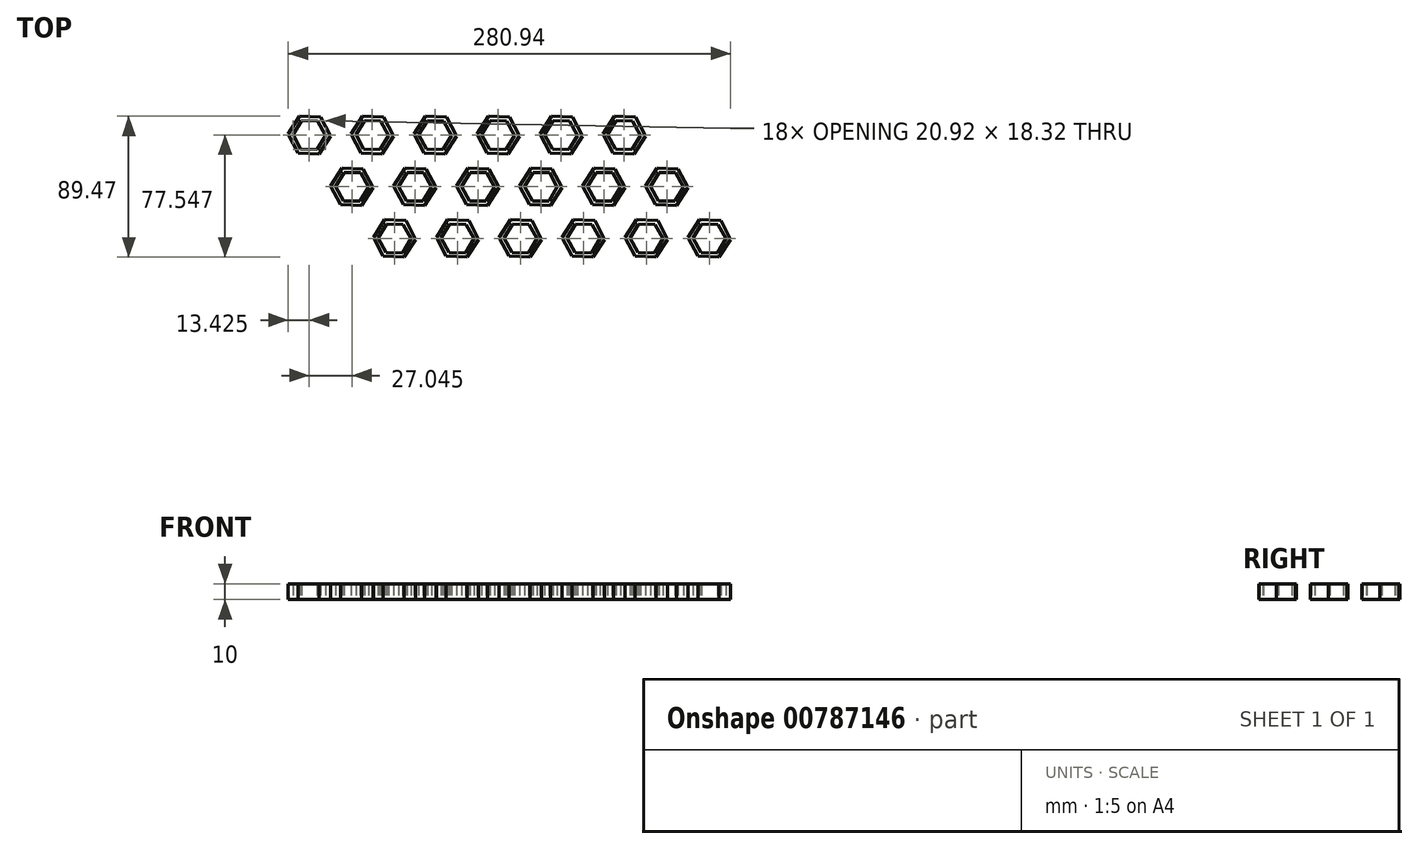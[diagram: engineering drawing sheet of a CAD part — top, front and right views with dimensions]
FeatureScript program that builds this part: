
annotation { "Feature Type Name" : "Feature", "Feature Type Description" : "" }
export const myFeature = defineFeature(function(context is Context, id is Id, definition is map)
    precondition{}
    {
        {
            var Q0;
            Q0=qCreatedBy(makeId("Top.planeOp"),FACE);
            var sketch = newSketch(context, id + "F0", { "sketchPlane" : qUnion([Q0])});
            skCircle(sketch, "E0.cCircle", {"center": v(-61.81, 33.14) * mm, "radius": 13.44 * mm, "construction": true});
            skLineSegment(sketch, "E0.0", {"start": v(-54.59, 44.46) * mm, "end": v(-48.4, 32.54) * mm});
            skLineSegment(sketch, "E0.1", {"start": v(-48.4, 32.54) * mm, "end": v(-55.62, 21.21) * mm});
            skLineSegment(sketch, "E0.2", {"start": v(-55.62, 21.21) * mm, "end": v(-69.04, 21.8) * mm});
            skLineSegment(sketch, "E0.3", {"start": v(-69.04, 21.8) * mm, "end": v(-75.24, 33.73) * mm});
            skLineSegment(sketch, "E0.4", {"start": v(-75.24, 33.73) * mm, "end": v(-68, 45.06) * mm});
            skLineSegment(sketch, "E0.5", {"start": v(-68, 45.06) * mm, "end": v(-54.59, 44.46) * mm});
            skCircle(sketch, "E1.cCircle", {"center": v(-61.81, 33.14) * mm, "radius": 10.46 * mm, "construction": true});
            skLineSegment(sketch, "E1.0", {"start": v(-56.75, 23.98) * mm, "end": v(-67.22, 24.17) * mm});
            skLineSegment(sketch, "E1.1", {"start": v(-67.22, 24.17) * mm, "end": v(-72.28, 33.33) * mm});
            skLineSegment(sketch, "E1.2", {"start": v(-72.28, 33.33) * mm, "end": v(-66.88, 42.3) * mm});
            skLineSegment(sketch, "E1.3", {"start": v(-66.88, 42.3) * mm, "end": v(-56.41, 42.1) * mm});
            skLineSegment(sketch, "E1.4", {"start": v(-56.41, 42.1) * mm, "end": v(-51.35, 32.94) * mm});
            skLineSegment(sketch, "E1.5", {"start": v(-51.35, 32.94) * mm, "end": v(-56.75, 23.98) * mm});
            skLineSegment(sketch, "E2.1.0.0", {"start": v(-11.35, 32.94) * mm, "end": v(-16.75, 23.98) * mm});
            skCircle(sketch, "E2.1.0.1", {"center": v(-21.81, 33.14) * mm, "radius": 13.44 * mm, "construction": true});
            skLineSegment(sketch, "E2.1.0.2", {"start": v(-14.59, 44.46) * mm, "end": v(-8.4, 32.54) * mm});
            skLineSegment(sketch, "E2.1.0.3", {"start": v(-8.4, 32.54) * mm, "end": v(-15.62, 21.21) * mm});
            skLineSegment(sketch, "E2.1.0.4", {"start": v(-15.62, 21.21) * mm, "end": v(-29.04, 21.8) * mm});
            skLineSegment(sketch, "E2.1.0.5", {"start": v(-29.04, 21.8) * mm, "end": v(-35.24, 33.73) * mm});
            skLineSegment(sketch, "E2.1.0.6", {"start": v(-35.24, 33.73) * mm, "end": v(-28, 45.06) * mm});
            skLineSegment(sketch, "E2.1.0.7", {"start": v(-28, 45.06) * mm, "end": v(-14.59, 44.46) * mm});
            skCircle(sketch, "E2.1.0.8", {"center": v(-21.81, 33.14) * mm, "radius": 10.46 * mm, "construction": true});
            skLineSegment(sketch, "E2.1.0.9", {"start": v(-16.75, 23.98) * mm, "end": v(-27.22, 24.17) * mm});
            skLineSegment(sketch, "E2.1.0.10", {"start": v(-27.22, 24.17) * mm, "end": v(-32.28, 33.33) * mm});
            skLineSegment(sketch, "E2.1.0.11", {"start": v(-32.28, 33.33) * mm, "end": v(-26.88, 42.3) * mm});
            skLineSegment(sketch, "E2.1.0.12", {"start": v(-26.88, 42.3) * mm, "end": v(-16.41, 42.1) * mm});
            skLineSegment(sketch, "E2.1.0.13", {"start": v(-16.41, 42.1) * mm, "end": v(-11.35, 32.94) * mm});
            skLineSegment(sketch, "E2.2.0.0", {"start": v(28.65, 32.94) * mm, "end": v(23.25, 23.98) * mm});
            skCircle(sketch, "E2.2.0.1", {"center": v(18.19, 33.14) * mm, "radius": 13.44 * mm, "construction": true});
            skLineSegment(sketch, "E2.2.0.2", {"start": v(25.41, 44.46) * mm, "end": v(31.6, 32.54) * mm});
            skLineSegment(sketch, "E2.2.0.3", {"start": v(31.6, 32.54) * mm, "end": v(24.38, 21.21) * mm});
            skLineSegment(sketch, "E2.2.0.4", {"start": v(24.38, 21.21) * mm, "end": v(10.96, 21.8) * mm});
            skLineSegment(sketch, "E2.2.0.5", {"start": v(10.96, 21.8) * mm, "end": v(4.76, 33.73) * mm});
            skLineSegment(sketch, "E2.2.0.6", {"start": v(4.76, 33.73) * mm, "end": v(12, 45.06) * mm});
            skLineSegment(sketch, "E2.2.0.7", {"start": v(12, 45.06) * mm, "end": v(25.41, 44.46) * mm});
            skCircle(sketch, "E2.2.0.8", {"center": v(18.19, 33.14) * mm, "radius": 10.46 * mm, "construction": true});
            skLineSegment(sketch, "E2.2.0.9", {"start": v(23.25, 23.98) * mm, "end": v(12.78, 24.17) * mm});
            skLineSegment(sketch, "E2.2.0.10", {"start": v(12.78, 24.17) * mm, "end": v(7.72, 33.33) * mm});
            skLineSegment(sketch, "E2.2.0.11", {"start": v(7.72, 33.33) * mm, "end": v(13.12, 42.3) * mm});
            skLineSegment(sketch, "E2.2.0.12", {"start": v(13.12, 42.3) * mm, "end": v(23.59, 42.1) * mm});
            skLineSegment(sketch, "E2.2.0.13", {"start": v(23.59, 42.1) * mm, "end": v(28.65, 32.94) * mm});
            skLineSegment(sketch, "E2.3.0.0", {"start": v(68.65, 32.94) * mm, "end": v(63.25, 23.98) * mm});
            skCircle(sketch, "E2.3.0.1", {"center": v(58.19, 33.14) * mm, "radius": 13.44 * mm, "construction": true});
            skLineSegment(sketch, "E2.3.0.2", {"start": v(65.41, 44.46) * mm, "end": v(71.6, 32.54) * mm});
            skLineSegment(sketch, "E2.3.0.3", {"start": v(71.6, 32.54) * mm, "end": v(64.38, 21.21) * mm});
            skLineSegment(sketch, "E2.3.0.4", {"start": v(64.38, 21.21) * mm, "end": v(50.96, 21.8) * mm});
            skLineSegment(sketch, "E2.3.0.5", {"start": v(50.96, 21.8) * mm, "end": v(44.76, 33.73) * mm});
            skLineSegment(sketch, "E2.3.0.6", {"start": v(44.76, 33.73) * mm, "end": v(52, 45.06) * mm});
            skLineSegment(sketch, "E2.3.0.7", {"start": v(52, 45.06) * mm, "end": v(65.41, 44.46) * mm});
            skCircle(sketch, "E2.3.0.8", {"center": v(58.19, 33.14) * mm, "radius": 10.46 * mm, "construction": true});
            skLineSegment(sketch, "E2.3.0.9", {"start": v(63.25, 23.98) * mm, "end": v(52.78, 24.17) * mm});
            skLineSegment(sketch, "E2.3.0.10", {"start": v(52.78, 24.17) * mm, "end": v(47.72, 33.33) * mm});
            skLineSegment(sketch, "E2.3.0.11", {"start": v(47.72, 33.33) * mm, "end": v(53.12, 42.3) * mm});
            skLineSegment(sketch, "E2.3.0.12", {"start": v(53.12, 42.3) * mm, "end": v(63.59, 42.1) * mm});
            skLineSegment(sketch, "E2.3.0.13", {"start": v(63.59, 42.1) * mm, "end": v(68.65, 32.94) * mm});
            skLineSegment(sketch, "E2.4.0.0", {"start": v(108.65, 32.94) * mm, "end": v(103.25, 23.98) * mm});
            skCircle(sketch, "E2.4.0.1", {"center": v(98.19, 33.14) * mm, "radius": 13.44 * mm, "construction": true});
            skLineSegment(sketch, "E2.4.0.2", {"start": v(105.41, 44.46) * mm, "end": v(111.6, 32.54) * mm});
            skLineSegment(sketch, "E2.4.0.3", {"start": v(111.6, 32.54) * mm, "end": v(104.38, 21.21) * mm});
            skLineSegment(sketch, "E2.4.0.4", {"start": v(104.38, 21.21) * mm, "end": v(90.96, 21.8) * mm});
            skLineSegment(sketch, "E2.4.0.5", {"start": v(90.96, 21.8) * mm, "end": v(84.76, 33.73) * mm});
            skLineSegment(sketch, "E2.4.0.6", {"start": v(84.76, 33.73) * mm, "end": v(92, 45.06) * mm});
            skLineSegment(sketch, "E2.4.0.7", {"start": v(92, 45.06) * mm, "end": v(105.41, 44.46) * mm});
            skCircle(sketch, "E2.4.0.8", {"center": v(98.19, 33.14) * mm, "radius": 10.46 * mm, "construction": true});
            skLineSegment(sketch, "E2.4.0.9", {"start": v(103.25, 23.98) * mm, "end": v(92.78, 24.17) * mm});
            skLineSegment(sketch, "E2.4.0.10", {"start": v(92.78, 24.17) * mm, "end": v(87.72, 33.33) * mm});
            skLineSegment(sketch, "E2.4.0.11", {"start": v(87.72, 33.33) * mm, "end": v(93.12, 42.3) * mm});
            skLineSegment(sketch, "E2.4.0.12", {"start": v(93.12, 42.3) * mm, "end": v(103.59, 42.1) * mm});
            skLineSegment(sketch, "E2.4.0.13", {"start": v(103.59, 42.1) * mm, "end": v(108.65, 32.94) * mm});
            skLineSegment(sketch, "E2.5.0.0", {"start": v(148.65, 32.94) * mm, "end": v(143.25, 23.98) * mm});
            skCircle(sketch, "E2.5.0.1", {"center": v(138.19, 33.14) * mm, "radius": 13.44 * mm, "construction": true});
            skLineSegment(sketch, "E2.5.0.2", {"start": v(145.41, 44.46) * mm, "end": v(151.6, 32.54) * mm});
            skLineSegment(sketch, "E2.5.0.3", {"start": v(151.6, 32.54) * mm, "end": v(144.38, 21.21) * mm});
            skLineSegment(sketch, "E2.5.0.4", {"start": v(144.38, 21.21) * mm, "end": v(130.96, 21.8) * mm});
            skLineSegment(sketch, "E2.5.0.5", {"start": v(130.96, 21.8) * mm, "end": v(124.76, 33.73) * mm});
            skLineSegment(sketch, "E2.5.0.6", {"start": v(124.76, 33.73) * mm, "end": v(132, 45.06) * mm});
            skLineSegment(sketch, "E2.5.0.7", {"start": v(132, 45.06) * mm, "end": v(145.41, 44.46) * mm});
            skCircle(sketch, "E2.5.0.8", {"center": v(138.19, 33.14) * mm, "radius": 10.46 * mm, "construction": true});
            skLineSegment(sketch, "E2.5.0.9", {"start": v(143.25, 23.98) * mm, "end": v(132.78, 24.17) * mm});
            skLineSegment(sketch, "E2.5.0.10", {"start": v(132.78, 24.17) * mm, "end": v(127.72, 33.33) * mm});
            skLineSegment(sketch, "E2.5.0.11", {"start": v(127.72, 33.33) * mm, "end": v(133.12, 42.3) * mm});
            skLineSegment(sketch, "E2.5.0.12", {"start": v(133.12, 42.3) * mm, "end": v(143.59, 42.1) * mm});
            skLineSegment(sketch, "E2.5.0.13", {"start": v(143.59, 42.1) * mm, "end": v(148.65, 32.94) * mm});
            skLineSegment(sketch, "E2.direction1", {"start": v(-69.04, 21.8) * mm, "end": v(-29.04, 21.8) * mm, "construction": true});
            skLineSegment(sketch, "E3.1.0.0", {"start": v(-42, -11) * mm, "end": v(-2, -11) * mm, "construction": true});
            skCircle(sketch, "E3.1.0.1", {"center": v(85.23, 0.33) * mm, "radius": 13.44 * mm, "construction": true});
            skCircle(sketch, "E3.1.0.2", {"center": v(125.23, 0.33) * mm, "radius": 13.44 * mm, "construction": true});
            skCircle(sketch, "E3.1.0.3", {"center": v(-34.77, 0.33) * mm, "radius": 13.44 * mm, "construction": true});
            skCircle(sketch, "E3.1.0.4", {"center": v(5.23, 0.33) * mm, "radius": 13.44 * mm, "construction": true});
            skCircle(sketch, "E3.1.0.5", {"center": v(45.23, 0.33) * mm, "radius": 13.44 * mm, "construction": true});
            skCircle(sketch, "E3.1.0.6", {"center": v(165.23, 0.33) * mm, "radius": 13.44 * mm, "construction": true});
            skLineSegment(sketch, "E3.1.0.7", {"start": v(92.46, 11.65) * mm, "end": v(98.65, -0.27) * mm});
            skLineSegment(sketch, "E3.1.0.8", {"start": v(90.63, 9.29) * mm, "end": v(95.7, 0.13) * mm});
            skLineSegment(sketch, "E3.1.0.9", {"start": v(159.04, 12.25) * mm, "end": v(172.46, 11.65) * mm});
            skLineSegment(sketch, "E3.1.0.10", {"start": v(-8.2, 0.92) * mm, "end": v(-0.96, 12.25) * mm});
            skLineSegment(sketch, "E3.1.0.11", {"start": v(158, -11) * mm, "end": v(151.8, 0.92) * mm});
            skLineSegment(sketch, "E3.1.0.12", {"start": v(10.63, 9.29) * mm, "end": v(15.7, 0.13) * mm});
            skLineSegment(sketch, "E3.1.0.13", {"start": v(138.65, -0.27) * mm, "end": v(131.42, -11.6) * mm});
            skLineSegment(sketch, "E3.1.0.14", {"start": v(39.04, 12.25) * mm, "end": v(52.46, 11.65) * mm});
            skLineSegment(sketch, "E3.1.0.15", {"start": v(90.3, -8.83) * mm, "end": v(79.83, -8.64) * mm});
            skLineSegment(sketch, "E3.1.0.16", {"start": v(114.77, 0.52) * mm, "end": v(120.17, 9.48) * mm});
            skLineSegment(sketch, "E3.1.0.17", {"start": v(170.63, 9.29) * mm, "end": v(175.7, 0.13) * mm});
            skLineSegment(sketch, "E3.1.0.18", {"start": v(12.46, 11.65) * mm, "end": v(18.65, -0.27) * mm});
            skLineSegment(sketch, "E3.1.0.19", {"start": v(-29.37, 9.29) * mm, "end": v(-24.3, 0.13) * mm});
            skLineSegment(sketch, "E3.1.0.20", {"start": v(159.83, -8.64) * mm, "end": v(154.77, 0.52) * mm});
            skCircle(sketch, "E3.1.0.21", {"center": v(125.23, 0.33) * mm, "radius": 10.46 * mm, "construction": true});
            skLineSegment(sketch, "E3.1.0.22", {"start": v(-39.83, 9.48) * mm, "end": v(-29.37, 9.29) * mm});
            skLineSegment(sketch, "E3.1.0.23", {"start": v(172.46, 11.65) * mm, "end": v(178.65, -0.27) * mm});
            skLineSegment(sketch, "E3.1.0.24", {"start": v(154.77, 0.52) * mm, "end": v(160.17, 9.48) * mm});
            skLineSegment(sketch, "E3.1.0.25", {"start": v(79.04, 12.25) * mm, "end": v(92.46, 11.65) * mm});
            skLineSegment(sketch, "E3.1.0.26", {"start": v(38, -11) * mm, "end": v(31.8, 0.92) * mm});
            skLineSegment(sketch, "E3.1.0.27", {"start": v(-45.23, 0.52) * mm, "end": v(-39.83, 9.48) * mm});
            skLineSegment(sketch, "E3.1.0.28", {"start": v(50.63, 9.29) * mm, "end": v(55.7, 0.13) * mm});
            skLineSegment(sketch, "E3.1.0.29", {"start": v(178.65, -0.27) * mm, "end": v(171.42, -11.6) * mm});
            skLineSegment(sketch, "E3.1.0.30", {"start": v(11.42, -11.6) * mm, "end": v(-2, -11) * mm});
            skLineSegment(sketch, "E3.1.0.31", {"start": v(160.17, 9.48) * mm, "end": v(170.63, 9.29) * mm});
            skLineSegment(sketch, "E3.1.0.32", {"start": v(119.83, -8.64) * mm, "end": v(114.77, 0.52) * mm});
            skLineSegment(sketch, "E3.1.0.33", {"start": v(-40.17, -8.64) * mm, "end": v(-45.23, 0.52) * mm});
            skLineSegment(sketch, "E3.1.0.34", {"start": v(-29.7, -8.83) * mm, "end": v(-40.17, -8.64) * mm});
            skLineSegment(sketch, "E3.1.0.35", {"start": v(50.3, -8.83) * mm, "end": v(39.83, -8.64) * mm});
            skLineSegment(sketch, "E3.1.0.36", {"start": v(52.46, 11.65) * mm, "end": v(58.65, -0.27) * mm});
            skLineSegment(sketch, "E3.1.0.37", {"start": v(74.77, 0.52) * mm, "end": v(80.17, 9.48) * mm});
            skLineSegment(sketch, "E3.1.0.38", {"start": v(130.63, 9.29) * mm, "end": v(135.7, 0.13) * mm});
            skCircle(sketch, "E3.1.0.39", {"center": v(-34.77, 0.33) * mm, "radius": 10.46 * mm, "construction": true});
            skLineSegment(sketch, "E3.1.0.40", {"start": v(151.8, 0.92) * mm, "end": v(159.04, 12.25) * mm});
            skLineSegment(sketch, "E3.1.0.41", {"start": v(131.42, -11.6) * mm, "end": v(118, -11) * mm});
            skCircle(sketch, "E3.1.0.42", {"center": v(45.23, 0.33) * mm, "radius": 10.46 * mm, "construction": true});
            skLineSegment(sketch, "E3.1.0.43", {"start": v(118, -11) * mm, "end": v(111.8, 0.92) * mm});
            skLineSegment(sketch, "E3.1.0.44", {"start": v(120.17, 9.48) * mm, "end": v(130.63, 9.29) * mm});
            skLineSegment(sketch, "E3.1.0.45", {"start": v(-40.96, 12.25) * mm, "end": v(-27.54, 11.65) * mm});
            skLineSegment(sketch, "E3.1.0.46", {"start": v(171.42, -11.6) * mm, "end": v(158, -11) * mm});
            skLineSegment(sketch, "E3.1.0.47", {"start": v(95.7, 0.13) * mm, "end": v(90.3, -8.83) * mm});
            skLineSegment(sketch, "E3.1.0.48", {"start": v(10.3, -8.83) * mm, "end": v(-0.17, -8.64) * mm});
            skLineSegment(sketch, "E3.1.0.49", {"start": v(-48.2, 0.92) * mm, "end": v(-40.96, 12.25) * mm});
            skLineSegment(sketch, "E3.1.0.50", {"start": v(-42, -11) * mm, "end": v(-48.2, 0.92) * mm});
            skLineSegment(sketch, "E3.1.0.51", {"start": v(71.8, 0.92) * mm, "end": v(79.04, 12.25) * mm});
            skLineSegment(sketch, "E3.1.0.52", {"start": v(-28.58, -11.6) * mm, "end": v(-42, -11) * mm});
            skLineSegment(sketch, "E3.1.0.53", {"start": v(-21.35, -0.27) * mm, "end": v(-28.58, -11.6) * mm});
            skLineSegment(sketch, "E3.1.0.54", {"start": v(130.3, -8.83) * mm, "end": v(119.83, -8.64) * mm});
            skLineSegment(sketch, "E3.1.0.55", {"start": v(-27.54, 11.65) * mm, "end": v(-21.35, -0.27) * mm});
            skLineSegment(sketch, "E3.1.0.56", {"start": v(-5.23, 0.52) * mm, "end": v(0.17, 9.48) * mm});
            skCircle(sketch, "E3.1.0.57", {"center": v(85.23, 0.33) * mm, "radius": 10.46 * mm, "construction": true});
            skLineSegment(sketch, "E3.1.0.58", {"start": v(31.8, 0.92) * mm, "end": v(39.04, 12.25) * mm});
            skLineSegment(sketch, "E3.1.0.59", {"start": v(15.7, 0.13) * mm, "end": v(10.3, -8.83) * mm});
            skLineSegment(sketch, "E3.1.0.60", {"start": v(58.65, -0.27) * mm, "end": v(51.42, -11.6) * mm});
            skLineSegment(sketch, "E3.1.0.61", {"start": v(91.42, -11.6) * mm, "end": v(78, -11) * mm});
            skLineSegment(sketch, "E3.1.0.62", {"start": v(-24.3, 0.13) * mm, "end": v(-29.7, -8.83) * mm});
            skLineSegment(sketch, "E3.1.0.63", {"start": v(111.8, 0.92) * mm, "end": v(119.04, 12.25) * mm});
            skLineSegment(sketch, "E3.1.0.64", {"start": v(39.83, -8.64) * mm, "end": v(34.77, 0.52) * mm});
            skLineSegment(sketch, "E3.1.0.65", {"start": v(80.17, 9.48) * mm, "end": v(90.63, 9.29) * mm});
            skCircle(sketch, "E3.1.0.66", {"center": v(165.23, 0.33) * mm, "radius": 10.46 * mm, "construction": true});
            skLineSegment(sketch, "E3.1.0.67", {"start": v(-0.96, 12.25) * mm, "end": v(12.46, 11.65) * mm});
            skLineSegment(sketch, "E3.1.0.68", {"start": v(55.7, 0.13) * mm, "end": v(50.3, -8.83) * mm});
            skLineSegment(sketch, "E3.1.0.69", {"start": v(175.7, 0.13) * mm, "end": v(170.3, -8.83) * mm});
            skLineSegment(sketch, "E3.1.0.70", {"start": v(78, -11) * mm, "end": v(71.8, 0.92) * mm});
            skLineSegment(sketch, "E3.1.0.71", {"start": v(119.04, 12.25) * mm, "end": v(132.46, 11.65) * mm});
            skLineSegment(sketch, "E3.1.0.72", {"start": v(170.3, -8.83) * mm, "end": v(159.83, -8.64) * mm});
            skCircle(sketch, "E3.1.0.73", {"center": v(5.23, 0.33) * mm, "radius": 10.46 * mm, "construction": true});
            skLineSegment(sketch, "E3.1.0.74", {"start": v(79.83, -8.64) * mm, "end": v(74.77, 0.52) * mm});
            skLineSegment(sketch, "E3.1.0.75", {"start": v(98.65, -0.27) * mm, "end": v(91.42, -11.6) * mm});
            skLineSegment(sketch, "E3.1.0.76", {"start": v(0.17, 9.48) * mm, "end": v(10.63, 9.29) * mm});
            skLineSegment(sketch, "E3.1.0.77", {"start": v(132.46, 11.65) * mm, "end": v(138.65, -0.27) * mm});
            skLineSegment(sketch, "E3.1.0.78", {"start": v(34.77, 0.52) * mm, "end": v(40.17, 9.48) * mm});
            skLineSegment(sketch, "E3.1.0.79", {"start": v(51.42, -11.6) * mm, "end": v(38, -11) * mm});
            skLineSegment(sketch, "E3.1.0.80", {"start": v(135.7, 0.13) * mm, "end": v(130.3, -8.83) * mm});
            skLineSegment(sketch, "E3.1.0.81", {"start": v(40.17, 9.48) * mm, "end": v(50.63, 9.29) * mm});
            skLineSegment(sketch, "E3.1.0.82", {"start": v(18.65, -0.27) * mm, "end": v(11.42, -11.6) * mm});
            skLineSegment(sketch, "E3.1.0.83", {"start": v(-0.17, -8.64) * mm, "end": v(-5.23, 0.52) * mm});
            skLineSegment(sketch, "E3.1.0.84", {"start": v(-2, -11) * mm, "end": v(-8.2, 0.92) * mm});
            skLineSegment(sketch, "E3.2.0.0", {"start": v(-14.96, -43.8) * mm, "end": v(25.04, -43.8) * mm, "construction": true});
            skCircle(sketch, "E3.2.0.1", {"center": v(112.27, -32.48) * mm, "radius": 13.44 * mm, "construction": true});
            skCircle(sketch, "E3.2.0.2", {"center": v(152.27, -32.48) * mm, "radius": 13.44 * mm, "construction": true});
            skCircle(sketch, "E3.2.0.3", {"center": v(-7.73, -32.48) * mm, "radius": 13.44 * mm, "construction": true});
            skCircle(sketch, "E3.2.0.4", {"center": v(32.27, -32.48) * mm, "radius": 13.44 * mm, "construction": true});
            skCircle(sketch, "E3.2.0.5", {"center": v(72.27, -32.48) * mm, "radius": 13.44 * mm, "construction": true});
            skCircle(sketch, "E3.2.0.6", {"center": v(192.27, -32.48) * mm, "radius": 13.44 * mm, "construction": true});
            skLineSegment(sketch, "E3.2.0.7", {"start": v(119.5, -21.16) * mm, "end": v(125.7, -33.08) * mm});
            skLineSegment(sketch, "E3.2.0.8", {"start": v(117.68, -23.52) * mm, "end": v(122.74, -32.68) * mm});
            skLineSegment(sketch, "E3.2.0.9", {"start": v(186.08, -20.56) * mm, "end": v(199.5, -21.16) * mm});
            skLineSegment(sketch, "E3.2.0.10", {"start": v(18.85, -31.89) * mm, "end": v(26.08, -20.56) * mm});
            skLineSegment(sketch, "E3.2.0.11", {"start": v(185.04, -43.8) * mm, "end": v(178.85, -31.89) * mm});
            skLineSegment(sketch, "E3.2.0.12", {"start": v(37.68, -23.52) * mm, "end": v(42.74, -32.68) * mm});
            skLineSegment(sketch, "E3.2.0.13", {"start": v(165.7, -33.08) * mm, "end": v(158.47, -44.4) * mm});
            skLineSegment(sketch, "E3.2.0.14", {"start": v(66.08, -20.56) * mm, "end": v(79.5, -21.16) * mm});
            skLineSegment(sketch, "E3.2.0.15", {"start": v(117.34, -41.64) * mm, "end": v(106.87, -41.44) * mm});
            skLineSegment(sketch, "E3.2.0.16", {"start": v(141.81, -32.29) * mm, "end": v(147.21, -23.33) * mm});
            skLineSegment(sketch, "E3.2.0.17", {"start": v(197.68, -23.52) * mm, "end": v(202.74, -32.68) * mm});
            skLineSegment(sketch, "E3.2.0.18", {"start": v(39.5, -21.16) * mm, "end": v(45.7, -33.08) * mm});
            skLineSegment(sketch, "E3.2.0.19", {"start": v(-2.32, -23.52) * mm, "end": v(2.74, -32.68) * mm});
            skLineSegment(sketch, "E3.2.0.20", {"start": v(186.87, -41.44) * mm, "end": v(181.81, -32.29) * mm});
            skCircle(sketch, "E3.2.0.21", {"center": v(152.27, -32.48) * mm, "radius": 10.46 * mm, "construction": true});
            skLineSegment(sketch, "E3.2.0.22", {"start": v(-12.79, -23.33) * mm, "end": v(-2.32, -23.52) * mm});
            skLineSegment(sketch, "E3.2.0.23", {"start": v(199.5, -21.16) * mm, "end": v(205.7, -33.08) * mm});
            skLineSegment(sketch, "E3.2.0.24", {"start": v(181.81, -32.29) * mm, "end": v(187.21, -23.33) * mm});
            skLineSegment(sketch, "E3.2.0.25", {"start": v(106.08, -20.56) * mm, "end": v(119.5, -21.16) * mm});
            skLineSegment(sketch, "E3.2.0.26", {"start": v(65.04, -43.8) * mm, "end": v(58.85, -31.89) * mm});
            skLineSegment(sketch, "E3.2.0.27", {"start": v(-18.19, -32.29) * mm, "end": v(-12.79, -23.33) * mm});
            skLineSegment(sketch, "E3.2.0.28", {"start": v(77.68, -23.52) * mm, "end": v(82.74, -32.68) * mm});
            skLineSegment(sketch, "E3.2.0.29", {"start": v(205.7, -33.08) * mm, "end": v(198.47, -44.4) * mm});
            skLineSegment(sketch, "E3.2.0.30", {"start": v(38.47, -44.4) * mm, "end": v(25.04, -43.8) * mm});
            skLineSegment(sketch, "E3.2.0.31", {"start": v(187.21, -23.33) * mm, "end": v(197.68, -23.52) * mm});
            skLineSegment(sketch, "E3.2.0.32", {"start": v(146.87, -41.44) * mm, "end": v(141.81, -32.29) * mm});
            skLineSegment(sketch, "E3.2.0.33", {"start": v(-13.13, -41.44) * mm, "end": v(-18.19, -32.29) * mm});
            skLineSegment(sketch, "E3.2.0.34", {"start": v(-2.66, -41.64) * mm, "end": v(-13.13, -41.44) * mm});
            skLineSegment(sketch, "E3.2.0.35", {"start": v(77.34, -41.64) * mm, "end": v(66.87, -41.44) * mm});
            skLineSegment(sketch, "E3.2.0.36", {"start": v(79.5, -21.16) * mm, "end": v(85.7, -33.08) * mm});
            skLineSegment(sketch, "E3.2.0.37", {"start": v(101.81, -32.29) * mm, "end": v(107.21, -23.33) * mm});
            skLineSegment(sketch, "E3.2.0.38", {"start": v(157.68, -23.52) * mm, "end": v(162.74, -32.68) * mm});
            skCircle(sketch, "E3.2.0.39", {"center": v(-7.73, -32.48) * mm, "radius": 10.46 * mm, "construction": true});
            skLineSegment(sketch, "E3.2.0.40", {"start": v(178.85, -31.89) * mm, "end": v(186.08, -20.56) * mm});
            skLineSegment(sketch, "E3.2.0.41", {"start": v(158.47, -44.4) * mm, "end": v(145.04, -43.8) * mm});
            skCircle(sketch, "E3.2.0.42", {"center": v(72.27, -32.48) * mm, "radius": 10.46 * mm, "construction": true});
            skLineSegment(sketch, "E3.2.0.43", {"start": v(145.04, -43.8) * mm, "end": v(138.85, -31.89) * mm});
            skLineSegment(sketch, "E3.2.0.44", {"start": v(147.21, -23.33) * mm, "end": v(157.68, -23.52) * mm});
            skLineSegment(sketch, "E3.2.0.45", {"start": v(-13.92, -20.56) * mm, "end": v(-0.5, -21.16) * mm});
            skLineSegment(sketch, "E3.2.0.46", {"start": v(198.47, -44.4) * mm, "end": v(185.04, -43.8) * mm});
            skLineSegment(sketch, "E3.2.0.47", {"start": v(122.74, -32.68) * mm, "end": v(117.34, -41.64) * mm});
            skLineSegment(sketch, "E3.2.0.48", {"start": v(37.34, -41.64) * mm, "end": v(26.87, -41.44) * mm});
            skLineSegment(sketch, "E3.2.0.49", {"start": v(-21.15, -31.89) * mm, "end": v(-13.92, -20.56) * mm});
            skLineSegment(sketch, "E3.2.0.50", {"start": v(-14.96, -43.8) * mm, "end": v(-21.15, -31.89) * mm});
            skLineSegment(sketch, "E3.2.0.51", {"start": v(98.85, -31.89) * mm, "end": v(106.08, -20.56) * mm});
            skLineSegment(sketch, "E3.2.0.52", {"start": v(-1.53, -44.4) * mm, "end": v(-14.96, -43.8) * mm});
            skLineSegment(sketch, "E3.2.0.53", {"start": v(5.7, -33.08) * mm, "end": v(-1.53, -44.4) * mm});
            skLineSegment(sketch, "E3.2.0.54", {"start": v(157.34, -41.64) * mm, "end": v(146.87, -41.44) * mm});
            skLineSegment(sketch, "E3.2.0.55", {"start": v(-0.5, -21.16) * mm, "end": v(5.7, -33.08) * mm});
            skLineSegment(sketch, "E3.2.0.56", {"start": v(21.81, -32.29) * mm, "end": v(27.21, -23.33) * mm});
            skCircle(sketch, "E3.2.0.57", {"center": v(112.27, -32.48) * mm, "radius": 10.46 * mm, "construction": true});
            skLineSegment(sketch, "E3.2.0.58", {"start": v(58.85, -31.89) * mm, "end": v(66.08, -20.56) * mm});
            skLineSegment(sketch, "E3.2.0.59", {"start": v(42.74, -32.68) * mm, "end": v(37.34, -41.64) * mm});
            skLineSegment(sketch, "E3.2.0.60", {"start": v(85.7, -33.08) * mm, "end": v(78.47, -44.4) * mm});
            skLineSegment(sketch, "E3.2.0.61", {"start": v(118.47, -44.4) * mm, "end": v(105.04, -43.8) * mm});
            skLineSegment(sketch, "E3.2.0.62", {"start": v(2.74, -32.68) * mm, "end": v(-2.66, -41.64) * mm});
            skLineSegment(sketch, "E3.2.0.63", {"start": v(138.85, -31.89) * mm, "end": v(146.08, -20.56) * mm});
            skLineSegment(sketch, "E3.2.0.64", {"start": v(66.87, -41.44) * mm, "end": v(61.81, -32.29) * mm});
            skLineSegment(sketch, "E3.2.0.65", {"start": v(107.21, -23.33) * mm, "end": v(117.68, -23.52) * mm});
            skCircle(sketch, "E3.2.0.66", {"center": v(192.27, -32.48) * mm, "radius": 10.46 * mm, "construction": true});
            skLineSegment(sketch, "E3.2.0.67", {"start": v(26.08, -20.56) * mm, "end": v(39.5, -21.16) * mm});
            skLineSegment(sketch, "E3.2.0.68", {"start": v(82.74, -32.68) * mm, "end": v(77.34, -41.64) * mm});
            skLineSegment(sketch, "E3.2.0.69", {"start": v(202.74, -32.68) * mm, "end": v(197.34, -41.64) * mm});
            skLineSegment(sketch, "E3.2.0.70", {"start": v(105.04, -43.8) * mm, "end": v(98.85, -31.89) * mm});
            skLineSegment(sketch, "E3.2.0.71", {"start": v(146.08, -20.56) * mm, "end": v(159.5, -21.16) * mm});
            skLineSegment(sketch, "E3.2.0.72", {"start": v(197.34, -41.64) * mm, "end": v(186.87, -41.44) * mm});
            skCircle(sketch, "E3.2.0.73", {"center": v(32.27, -32.48) * mm, "radius": 10.46 * mm, "construction": true});
            skLineSegment(sketch, "E3.2.0.74", {"start": v(106.87, -41.44) * mm, "end": v(101.81, -32.29) * mm});
            skLineSegment(sketch, "E3.2.0.75", {"start": v(125.7, -33.08) * mm, "end": v(118.47, -44.4) * mm});
            skLineSegment(sketch, "E3.2.0.76", {"start": v(27.21, -23.33) * mm, "end": v(37.68, -23.52) * mm});
            skLineSegment(sketch, "E3.2.0.77", {"start": v(159.5, -21.16) * mm, "end": v(165.7, -33.08) * mm});
            skLineSegment(sketch, "E3.2.0.78", {"start": v(61.81, -32.29) * mm, "end": v(67.21, -23.33) * mm});
            skLineSegment(sketch, "E3.2.0.79", {"start": v(78.47, -44.4) * mm, "end": v(65.04, -43.8) * mm});
            skLineSegment(sketch, "E3.2.0.80", {"start": v(162.74, -32.68) * mm, "end": v(157.34, -41.64) * mm});
            skLineSegment(sketch, "E3.2.0.81", {"start": v(67.21, -23.33) * mm, "end": v(77.68, -23.52) * mm});
            skLineSegment(sketch, "E3.2.0.82", {"start": v(45.7, -33.08) * mm, "end": v(38.47, -44.4) * mm});
            skLineSegment(sketch, "E3.2.0.83", {"start": v(26.87, -41.44) * mm, "end": v(21.81, -32.29) * mm});
            skLineSegment(sketch, "E3.2.0.84", {"start": v(25.04, -43.8) * mm, "end": v(18.85, -31.89) * mm});
            skLineSegment(sketch, "E3.direction1", {"start": v(-69.04, 21.8) * mm, "end": v(-42, -11) * mm, "construction": true});
            skSolve(sketch);
        }
        {
            var Q0;
            Q0=makeQuery(id+"F0.imprint","IMPRINT",FACE,{"disambiguationData":[TD([[makeQuery(id+"F0.imprint","IMPRINT",EDGE,{"derivedFrom":sQuery(id+"F0.wireOp",EDGE,"E0.0")}),-1.0]])]});
            var Q1;
            Q1=makeQuery(id+"F0.imprint","IMPRINT",FACE,{"disambiguationData":[TD([[makeQuery(id+"F0.imprint","IMPRINT",EDGE,{"derivedFrom":sQuery(id+"F0.wireOp",EDGE,"E2.1.0.0")}),1.0]])]});
            var Q2;
            Q2=makeQuery(id+"F0.imprint","IMPRINT",FACE,{"disambiguationData":[TD([[makeQuery(id+"F0.imprint","IMPRINT",EDGE,{"derivedFrom":sQuery(id+"F0.wireOp",EDGE,"E2.2.0.0")}),1.0]])]});
            var Q3;
            Q3=makeQuery(id+"F0.imprint","IMPRINT",FACE,{"disambiguationData":[TD([[makeQuery(id+"F0.imprint","IMPRINT",EDGE,{"derivedFrom":sQuery(id+"F0.wireOp",EDGE,"E2.3.0.0")}),1.0]])]});
            var Q4;
            Q4=makeQuery(id+"F0.imprint","IMPRINT",FACE,{"disambiguationData":[TD([[makeQuery(id+"F0.imprint","IMPRINT",EDGE,{"derivedFrom":sQuery(id+"F0.wireOp",EDGE,"E2.4.0.0")}),1.0]])]});
            var Q5;
            Q5=makeQuery(id+"F0.imprint","IMPRINT",FACE,{"disambiguationData":[TD([[makeQuery(id+"F0.imprint","IMPRINT",EDGE,{"derivedFrom":sQuery(id+"F0.wireOp",EDGE,"E2.5.0.0")}),1.0]])]});
            var Q6;
            Q6=makeQuery(id+"F0.imprint","IMPRINT",FACE,{"disambiguationData":[TD([[makeQuery(id+"F0.imprint","IMPRINT",EDGE,{"derivedFrom":sQuery(id+"F0.wireOp",EDGE,"E3.1.0.9")}),-1.0]])]});
            var Q7;
            Q7=makeQuery(id+"F0.imprint","IMPRINT",FACE,{"disambiguationData":[TD([[makeQuery(id+"F0.imprint","IMPRINT",EDGE,{"derivedFrom":sQuery(id+"F0.wireOp",EDGE,"E3.1.0.13")}),-1.0]])]});
            var Q8;
            Q8=makeQuery(id+"F0.imprint","IMPRINT",FACE,{"disambiguationData":[TD([[makeQuery(id+"F0.imprint","IMPRINT",EDGE,{"derivedFrom":sQuery(id+"F0.wireOp",EDGE,"E3.1.0.7")}),-1.0]])]});
            var Q9;
            Q9=makeQuery(id+"F0.imprint","IMPRINT",FACE,{"disambiguationData":[TD([[makeQuery(id+"F0.imprint","IMPRINT",EDGE,{"derivedFrom":sQuery(id+"F0.wireOp",EDGE,"E3.1.0.14")}),-1.0]])]});
            var Q10;
            Q10=makeQuery(id+"F0.imprint","IMPRINT",FACE,{"disambiguationData":[TD([[makeQuery(id+"F0.imprint","IMPRINT",EDGE,{"derivedFrom":sQuery(id+"F0.wireOp",EDGE,"E3.1.0.10")}),-1.0]])]});
            var Q11;
            Q11=makeQuery(id+"F0.imprint","IMPRINT",FACE,{"disambiguationData":[TD([[makeQuery(id+"F0.imprint","IMPRINT",EDGE,{"derivedFrom":sQuery(id+"F0.wireOp",EDGE,"E3.1.0.19")}),1.0]])]});
            var Q12;
            Q12=makeQuery(id+"F0.imprint","IMPRINT",FACE,{"disambiguationData":[TD([[makeQuery(id+"F0.imprint","IMPRINT",EDGE,{"derivedFrom":sQuery(id+"F0.wireOp",EDGE,"E3.2.0.19")}),1.0]])]});
            var Q13;
            Q13=makeQuery(id+"F0.imprint","IMPRINT",FACE,{"disambiguationData":[TD([[makeQuery(id+"F0.imprint","IMPRINT",EDGE,{"derivedFrom":sQuery(id+"F0.wireOp",EDGE,"E3.2.0.10")}),-1.0]])]});
            var Q14;
            Q14=makeQuery(id+"F0.imprint","IMPRINT",FACE,{"disambiguationData":[TD([[makeQuery(id+"F0.imprint","IMPRINT",EDGE,{"derivedFrom":sQuery(id+"F0.wireOp",EDGE,"E3.2.0.14")}),-1.0]])]});
            var Q15;
            Q15=makeQuery(id+"F0.imprint","IMPRINT",FACE,{"disambiguationData":[TD([[makeQuery(id+"F0.imprint","IMPRINT",EDGE,{"derivedFrom":sQuery(id+"F0.wireOp",EDGE,"E3.2.0.7")}),-1.0]])]});
            var Q16;
            Q16=makeQuery(id+"F0.imprint","IMPRINT",FACE,{"disambiguationData":[TD([[makeQuery(id+"F0.imprint","IMPRINT",EDGE,{"derivedFrom":sQuery(id+"F0.wireOp",EDGE,"E3.2.0.13")}),-1.0]])]});
            var Q17;
            Q17=makeQuery(id+"F0.imprint","IMPRINT",FACE,{"disambiguationData":[TD([[makeQuery(id+"F0.imprint","IMPRINT",EDGE,{"derivedFrom":sQuery(id+"F0.wireOp",EDGE,"E3.2.0.9")}),-1.0]])]});
            extrude(context, id + "F1", {"entities" : qUnion([Q0, Q1, Q2, Q3, Q4, Q5, Q6, Q7, Q8, Q9, Q10, Q11, Q12, Q13, Q14, Q15, Q16, Q17]), "depth" : 10 * mm, "offsetDistance" : 25 * mm});
        }
    });
